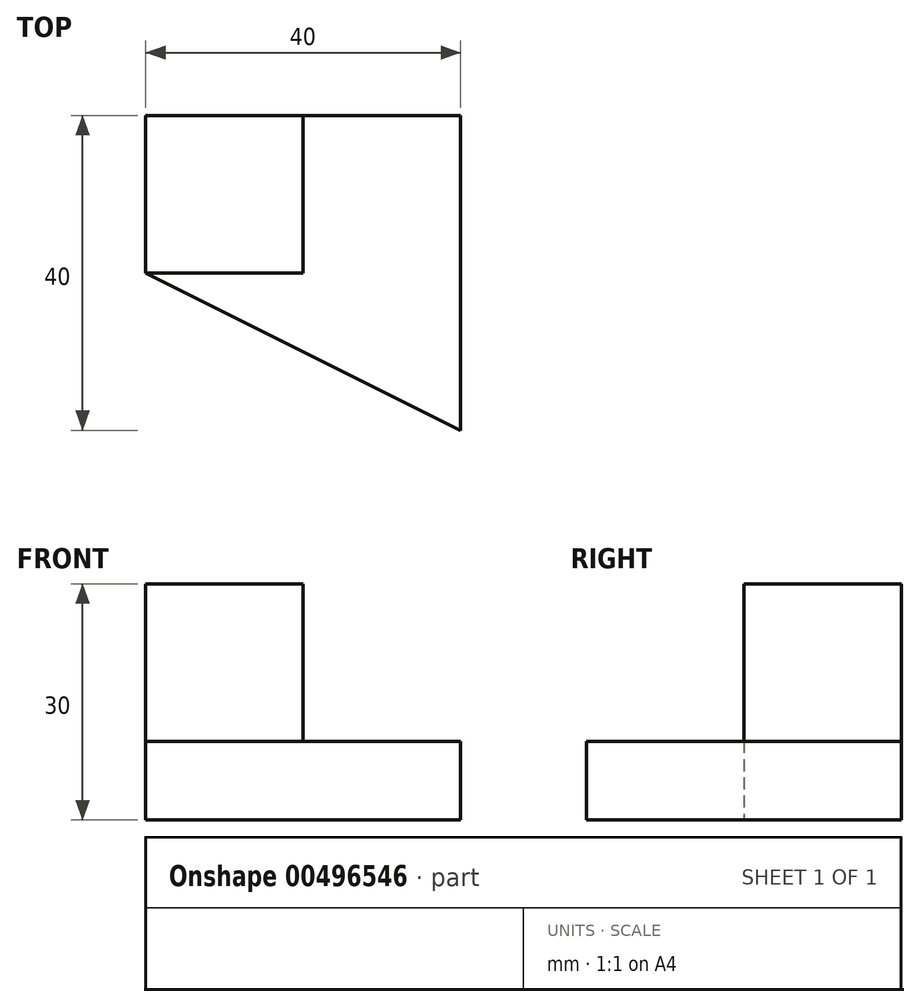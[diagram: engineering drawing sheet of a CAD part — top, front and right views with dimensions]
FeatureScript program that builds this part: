
annotation { "Feature Type Name" : "Feature", "Feature Type Description" : "" }
export const myFeature = defineFeature(function(context is Context, id is Id, definition is map)
    precondition{}
    {
        {
            var Q0;
            Q0=qCreatedBy(makeId("Top.planeOp"),FACE);
            var sketch = newSketch(context, id + "F0", { "sketchPlane" : qUnion([Q0])});
            skLineSegment(sketch, "E0", {"start": v(0, 0) * mm, "end": v(0, 20) * mm});
            skLineSegment(sketch, "E1", {"start": v(0, 20) * mm, "end": v(40, 20) * mm});
            skLineSegment(sketch, "E2", {"start": v(40, 20) * mm, "end": v(40, -20) * mm});
            skLineSegment(sketch, "E3", {"start": v(0, 0) * mm, "end": v(40, -20) * mm});
            skSolve(sketch);
        }
        {
            var Q0;
            Q0 = qSketchRegion(id + "F0", true);
            extrude(context, id + "F1", {"entities" : qUnion([Q0]), "depth" : 10 * mm});
        }
        {
            var Q0;
            Q0=makeQuery(id+"F1.opExtrude","CAP_FACE",FACE,{"disambiguationData":[OSD([sQuery(id+"F0.wireOp",EDGE,"E0"),sQuery(id+"F0.wireOp",EDGE,"E1"),sQuery(id+"F0.wireOp",EDGE,"E2"),sQuery(id+"F0.wireOp",EDGE,"E3")])],"isStart":false});
            var sketch = newSketch(context, id + "F2", { "sketchPlane" : qUnion([Q0])});
            skLineSegment(sketch, "E4", {"start": v(0, 0) * mm, "end": v(20, 0) * mm});
            skLineSegment(sketch, "E5", {"start": v(20, 0) * mm, "end": v(20, 20) * mm});
            skSolve(sketch);
        }
        {
            var Q0;
            Q0=makeQuery(id+"F2.imprint","IMPRINT",FACE,{"disambiguationData":[TD([[makeQuery(id+"F2.imprint","IMPRINT",EDGE,{"derivedFrom":sQuery(id+"F2.wireOp",EDGE,"E4")}),1.0]])]});
            extrude(context, id + "F3", {"entities" : qUnion([Q0]), "operationType" : NewBodyOperationType.ADD, "depth" : 20 * mm});
        }
    });
